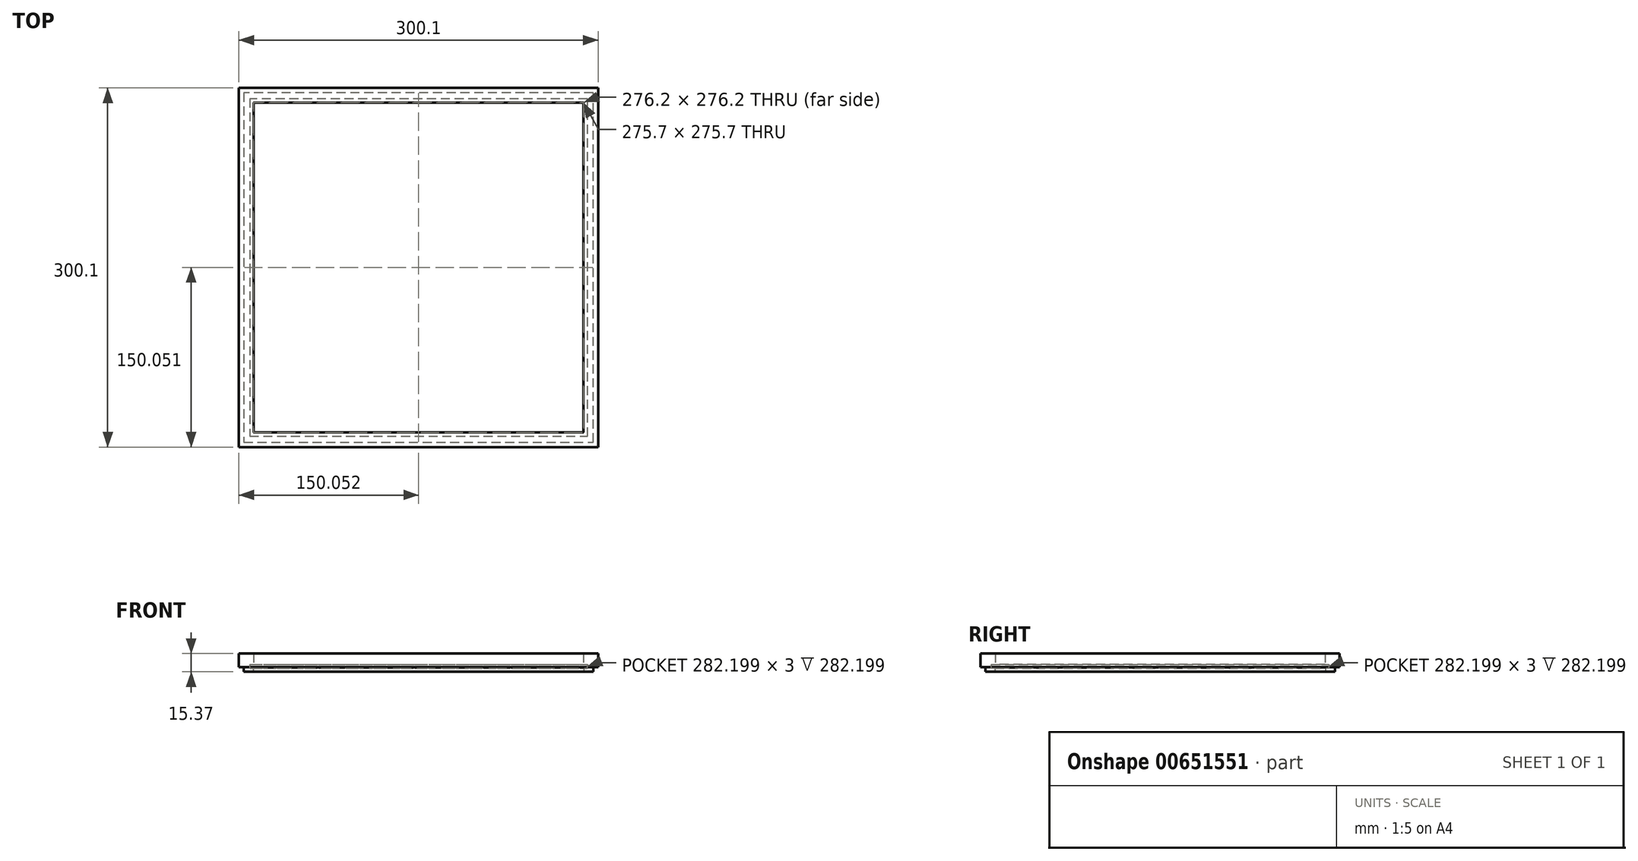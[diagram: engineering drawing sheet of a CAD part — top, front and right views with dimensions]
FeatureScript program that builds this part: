
annotation { "Feature Type Name" : "Feature", "Feature Type Description" : "" }
export const myFeature = defineFeature(function(context is Context, id is Id, definition is map)
    precondition{}
    {
        {
            var Q0;
            Q0=qCreatedBy(makeId("Top.planeOp"),FACE);
            var sketch = newSketch(context, id + "F0", { "sketchPlane" : qUnion([Q0])});
            skLineSegment(sketch, "E0.bottom", {"start": v(-143.73, -156.8) * mm, "end": v(156.27, -156.8) * mm});
            skLineSegment(sketch, "E0.top", {"start": v(-143.73, 143.2) * mm, "end": v(156.27, 143.2) * mm});
            skLineSegment(sketch, "E0.left", {"start": v(-143.73, -156.8) * mm, "end": v(-143.73, 143.2) * mm});
            skLineSegment(sketch, "E0.right", {"start": v(156.27, -156.8) * mm, "end": v(156.27, 143.2) * mm});
            skSolve(sketch);
        }
        {
            var Q0;
            Q0=qCreatedBy(makeId("Right.planeOp"),FACE);
            var sketch = newSketch(context, id + "F1", { "sketchPlane" : qUnion([Q0])});
            skLineSegment(sketch, "E1", {"start": v(-144.9, -0.35) * mm, "end": v(-144.9, 2.65) * mm});
            skLineSegment(sketch, "E2", {"start": v(-144.9, 2.65) * mm, "end": v(-147.9, 2.65) * mm});
            skLineSegment(sketch, "E3", {"start": v(-147.9, 2.65) * mm, "end": v(-147.9, 5.65) * mm});
            skLineSegment(sketch, "E4", {"start": v(-147.9, 5.65) * mm, "end": v(-144.65, 5.65) * mm});
            skLineSegment(sketch, "E5", {"start": v(-144.65, 5.65) * mm, "end": v(-144.65, 15.02) * mm});
            skLineSegment(sketch, "E6", {"start": v(-144.65, 15.02) * mm, "end": v(-156.85, 15.02) * mm});
            skLineSegment(sketch, "E7", {"start": v(-156.85, 3.65) * mm, "end": v(-152.85, 3.65) * mm});
            skLineSegment(sketch, "E8", {"start": v(-152.85, -0.35) * mm, "end": v(-152.85, 3.65) * mm});
            skLineSegment(sketch, "E9", {"start": v(-156.85, 3.65) * mm, "end": v(-156.85, 15.02) * mm});
            skLineSegment(sketch, "E10", {"start": v(-152.85, -0.35) * mm, "end": v(-144.9, -0.35) * mm});
            skSolve(sketch);
        }
        {
            var Q0;
            Q0=makeQuery(id+"F1.imprint","IMPRINT",FACE,{"disambiguationData":[TD([[makeQuery(id+"F1.imprint","IMPRINT",EDGE,{"derivedFrom":sQuery(id+"F1.wireOp",EDGE,"E1")}),1.0]])]});
            var Q1;
            Q1=sQuery(id+"F0.wireOp",EDGE,"E0.bottom");
            var Q2;
            Q2=sQuery(id+"F0.wireOp",EDGE,"E0.left");
            var Q3;
            Q3=sQuery(id+"F0.wireOp",EDGE,"E0.right");
            var Q4;
            Q4=sQuery(id+"F0.wireOp",EDGE,"E0.top");
            sweep(context, id + "F2", {"profiles" : qUnion([Q0]), "path" : qUnion([Q1, Q2, Q3, Q4])});
        }
    });
